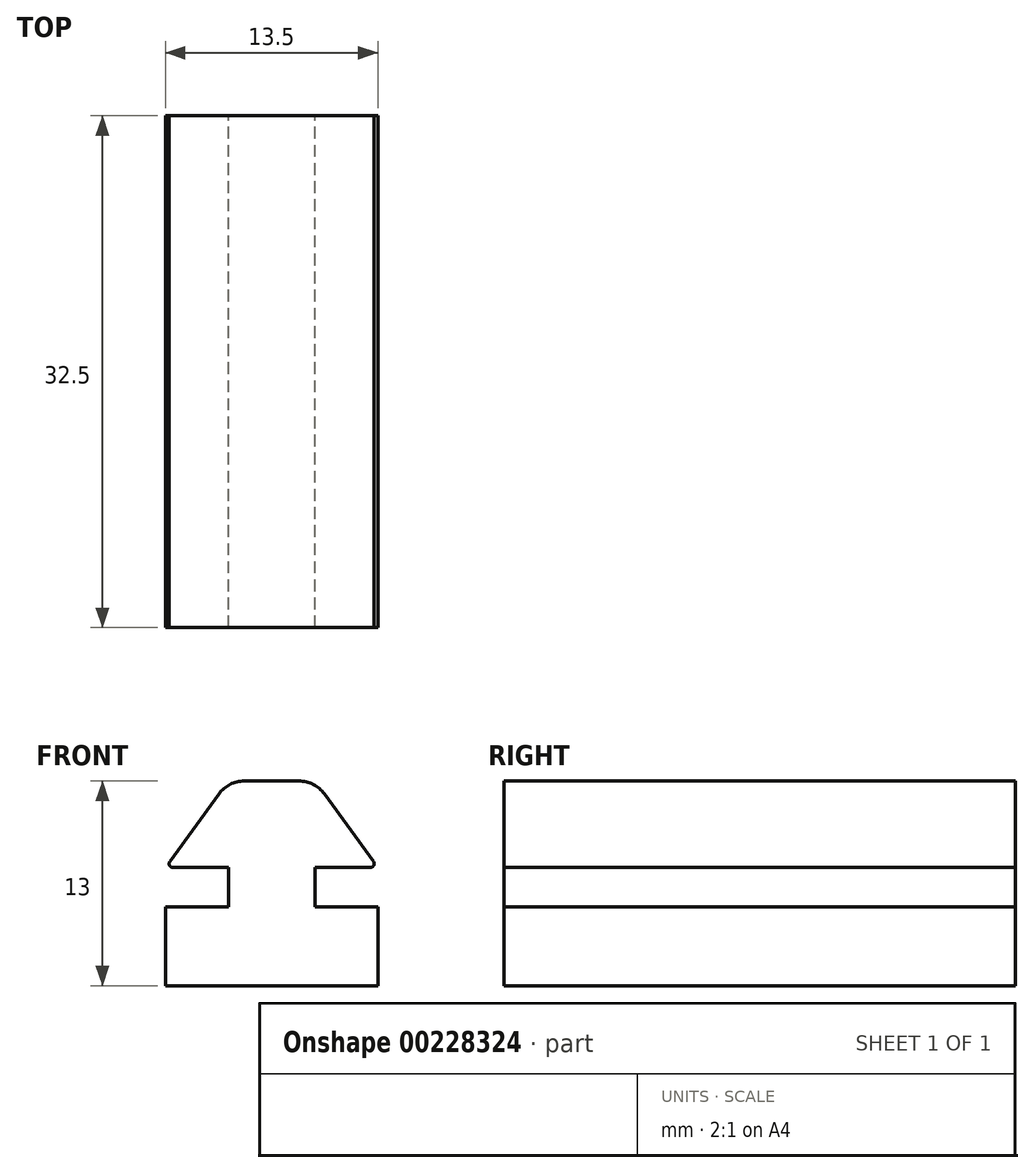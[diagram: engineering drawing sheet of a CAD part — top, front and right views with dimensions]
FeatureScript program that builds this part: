
annotation { "Feature Type Name" : "Feature", "Feature Type Description" : "" }
export const myFeature = defineFeature(function(context is Context, id is Id, definition is map)
    precondition{}
    {
        {
            var Q0;
            Q0=qCreatedBy(makeId("Front.planeOp"),FACE);
            var sketch = newSketch(context, id + "F0", { "sketchPlane" : qUnion([Q0])});
            skLineSegment(sketch, "E0", {"start": v(-6.75, 0) * mm, "end": v(6.75, 0) * mm});
            skLineSegment(sketch, "E1", {"start": v(0, 0) * mm, "end": v(0, 5.5) * mm});
            skLineSegment(sketch, "E2", {"start": v(0, 5.5) * mm, "end": v(-2.75, 5.5) * mm});
            skLineSegment(sketch, "E3", {"start": v(-2.75, 5.5) * mm, "end": v(2.75, 5.5) * mm});
            skLineSegment(sketch, "E4", {"start": v(-6.75, 0) * mm, "end": v(-2.75, 5.5) * mm});
            skLineSegment(sketch, "E5", {"start": v(2.75, 5.5) * mm, "end": v(6.75, 0) * mm});
            skLineSegment(sketch, "E6", {"start": v(-2.75, 5.5) * mm, "end": v(-2.75, -2.5) * mm});
            skLineSegment(sketch, "E7", {"start": v(2.75, 5.5) * mm, "end": v(2.75, -2.5) * mm});
            skLineSegment(sketch, "E8", {"start": v(-2.75, -2.5) * mm, "end": v(-6.75, -2.5) * mm});
            skLineSegment(sketch, "E9", {"start": v(-6.75, -2.5) * mm, "end": v(-6.75, -7.5) * mm});
            skLineSegment(sketch, "E10", {"start": v(2.75, -2.5) * mm, "end": v(6.75, -2.5) * mm});
            skLineSegment(sketch, "E11", {"start": v(-6.75, -7.5) * mm, "end": v(6.75, -7.5) * mm});
            skLineSegment(sketch, "E12", {"start": v(6.75, -2.5) * mm, "end": v(6.75, -7.5) * mm});
            skSolve(sketch);
        }
        {
            var Q0;
            {var subQ0=sQuery(id+"F0.wireOp",EDGE,"E1");Q0=makeQuery(id+"F0.imprint","IMPRINT",FACE,{"disambiguationData":[TD([[makeQuery(id+"F0.imprint","IMPRINT",EDGE,{"derivedFrom":subQ0}),-1.0]])]});}
            var Q1;
            {var subQ4=sQuery(id+"F0.wireOp",EDGE,"E8");Q1=makeQuery(id+"F0.imprint","IMPRINT",FACE,{"disambiguationData":[TD([[makeQuery(id+"F0.imprint","IMPRINT",EDGE,{"derivedFrom":subQ4}),1.0]])]});}
            var Q2;
            {var subQ0=sQuery(id+"F0.wireOp",EDGE,"E5");Q2=makeQuery(id+"F0.imprint","IMPRINT",FACE,{"disambiguationData":[TD([[makeQuery(id+"F0.imprint","IMPRINT",EDGE,{"derivedFrom":subQ0}),-1.0]])]});}
            var Q3;
            {var subQ0=sQuery(id+"F0.wireOp",EDGE,"E1");Q3=makeQuery(id+"F0.imprint","IMPRINT",FACE,{"disambiguationData":[TD([[makeQuery(id+"F0.imprint","IMPRINT",EDGE,{"derivedFrom":subQ0}),1.0]])]});}
            var Q4;
            {var subQ0=sQuery(id+"F0.wireOp",EDGE,"E4");Q4=makeQuery(id+"F0.imprint","IMPRINT",FACE,{"disambiguationData":[TD([[makeQuery(id+"F0.imprint","IMPRINT",EDGE,{"derivedFrom":subQ0}),-1.0]])]});}
            extrude(context, id + "F1", {"entities" : qUnion([Q0, Q1, Q2, Q3, Q4]), "depth" : 32.5 * mm});
        }
        {
            var Q0;
            Q0=makeQuery(id+"F1.opExtrude","SWEPT_EDGE",EDGE,{"disambiguationData":[OSD([sQuery(id+"F0.wireOp",EDGE,"E3"),sQuery(id+"F0.wireOp",EDGE,"E5"),sQuery(id+"F0.wireOp",EDGE,"E7")])]});
            var Q1;
            Q1=makeQuery(id+"F1.opExtrude","SWEPT_EDGE",EDGE,{"disambiguationData":[OSD([sQuery(id+"F0.wireOp",EDGE,"E3"),sQuery(id+"F0.wireOp",EDGE,"E4"),sQuery(id+"F0.wireOp",EDGE,"E6")])]});
            fillet(context, id + "F2", {"entities" : qUnion([Q0, Q1]), "radius" : 2 * mm, "tangentPropagation" : true, "allowEdgeOverflow" : false});
        }
        {
            var Q0;
            Q0=makeQuery(id+"F1.opExtrude","SWEPT_EDGE",EDGE,{"disambiguationData":[OSD([sQuery(id+"F0.wireOp",EDGE,"E0"),sQuery(id+"F0.wireOp",EDGE,"E5")])]});
            var Q1;
            Q1=makeQuery(id+"F1.opExtrude","SWEPT_EDGE",EDGE,{"disambiguationData":[OSD([sQuery(id+"F0.wireOp",EDGE,"E0"),sQuery(id+"F0.wireOp",EDGE,"E4")])]});
            fillet(context, id + "F3", {"entities" : qUnion([Q0, Q1]), "radius" : .25 * mm, "tangentPropagation" : true, "allowEdgeOverflow" : false});
        }
    });
